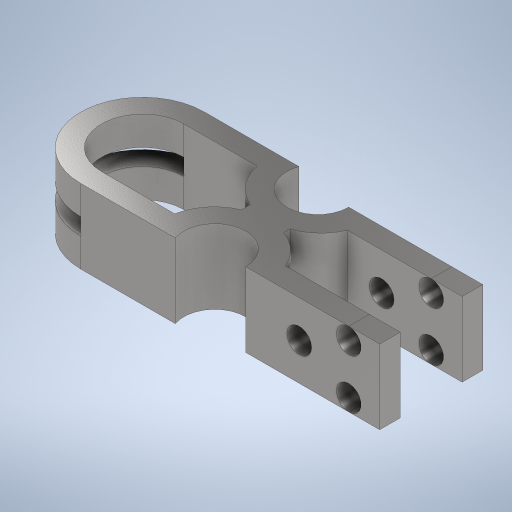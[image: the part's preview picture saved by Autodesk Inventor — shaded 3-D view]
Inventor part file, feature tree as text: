
AUTODESK INVENTOR PART (.ipt)
format: ipt  version: 2024 (Build 280153000, 153)  size: 342,528 bytes
history: native  units: mm
features: sketch x3, extrude x2, hole x1, plane x1
ambient origin geometry x8: Origin, YZ Plane, XZ Plane, XY Plane, X Axis, Y Axis, Z Axis, Center Point
bodies: Volumenkörper1 (feature_tree)
feature tree (7):
  extrude  "Extrusion1"  Depth=50.0mm
  hole  "Bohrung1"  [1 undecoded]
  plane  "Arbeitsebene1"
  extrude  "Extrusion2"  Depth=15.0mm
  sketch  "Skizze1"  dims[d17=30.0mm d18=50.0mm]
  sketch  "Skizze2"  dims[d19=25.0mm d20=3.0mm]
  sketch  "Skizze3"  dims[d21=80.0mm d28=15.0mm d30=30.0mm d34=20.0mm d36=25.0mm d37=25.0mm d38=60.0mm d39=20.0mm d40=36.0mm d41=0.0mm d42=24.0mm d43=6.0mm d44=24.0mm d45=15.0mm d46=12.0mm d47=6.0mm d48=4.0mm d49=2.0mm d50=90.0deg d51=8.0mm d52=0.0mm d53=18.0mm d54=30.0mm d55=8.0mm d56=0.0mm]
note: 1 required parameter value undecoded (feature->parameter linkage not recoverable at this tier; creation-order binding heuristic only, values carry confidence <= 0.55)
